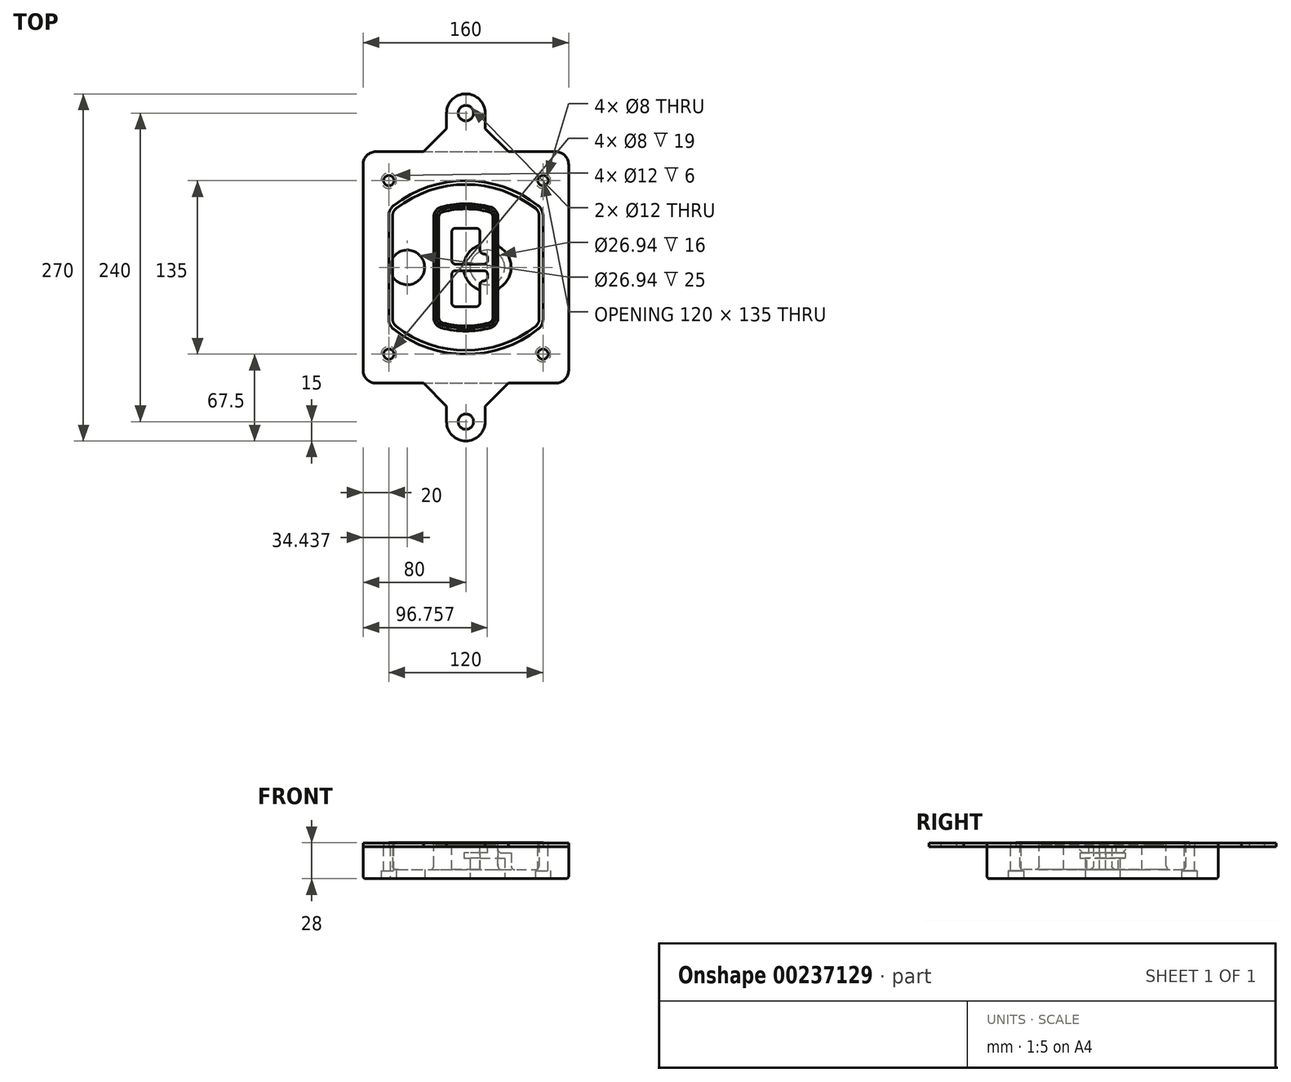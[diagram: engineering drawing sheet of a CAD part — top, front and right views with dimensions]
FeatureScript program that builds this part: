
annotation { "Feature Type Name" : "Feature", "Feature Type Description" : "" }
export const myFeature = defineFeature(function(context is Context, id is Id, definition is map)
    precondition{}
    {
        {
            var Q0;
            Q0=qCreatedBy(makeId("Top.planeOp"),FACE);
            var sketch = newSketch(context, id + "F0", { "sketchPlane" : qUnion([Q0])});
            skPoint(sketch, "E0.rect.middle", {"position": v(0, 0) * mm});
            skLineSegment(sketch, "E1.bottom", {"start": v(-70, -90) * mm, "end": v(70, -90) * mm});
            skLineSegment(sketch, "E1.top", {"start": v(-70, 90) * mm, "end": v(70, 90) * mm});
            skLineSegment(sketch, "E1.left", {"start": v(-80, -80) * mm, "end": v(-80, 80) * mm});
            skLineSegment(sketch, "E1.right", {"start": v(80, -80) * mm, "end": v(80, 80) * mm});
            skLineSegment(sketch, "E2", {"start": v(-80, 90) * mm, "end": v(80, -90) * mm, "construction": true});
            skLineSegment(sketch, "E3", {"start": v(80, 90) * mm, "end": v(-80, -90) * mm, "construction": true});
            skCircle(sketch, "E4", {"center": v(-60, 67.5) * mm, "radius": 4 * mm});
            skCircle(sketch, "E5", {"center": v(60, 67.5) * mm, "radius": 4 * mm});
            skCircle(sketch, "E6", {"center": v(60, -67.5) * mm, "radius": 4 * mm});
            skCircle(sketch, "E7", {"center": v(-60, -67.5) * mm, "radius": 4 * mm});
            skLineSegment(sketch, "E8", {"start": v(-60, 67.5) * mm, "end": v(60, 67.5) * mm, "construction": true});
            skLineSegment(sketch, "E9", {"start": v(60, 67.5) * mm, "end": v(60, -67.5) * mm, "construction": true});
            skLineSegment(sketch, "E10", {"start": v(60, -67.5) * mm, "end": v(-60, -67.5) * mm, "construction": true});
            skLineSegment(sketch, "E11", {"start": v(-60, -67.5) * mm, "end": v(-60, 67.5) * mm, "construction": true});
            skLineSegment(sketch, "E12", {"start": v(-60, 40.3) * mm, "end": v(-60, -40.3) * mm});
            skLineSegment(sketch, "E13", {"start": v(60, 40.3) * mm, "end": v(60, -40.3) * mm});
            skArc(sketch, "E14", {"start": v(56.15, 48.18) * mm, "mid": v(0, 67.5) * mm, "end": v(-56.15, 48.18) * mm});
            skArc(sketch, "E15", {"start": v(-56.15, -48.18) * mm, "mid": v(0, -67.5) * mm, "end": v(56.15, -48.18) * mm});
            skLineSegment(sketch, "E16", {"start": v(-60, 0) * mm, "end": v(60, 0) * mm, "construction": true});
            skPoint(sketch, "E17.visualSharp", {"position": v(-60, -45) * mm});
            skArc(sketch, "E17.filletArc", {"start": v(-60, -40.3) * mm, "mid": v(-58.99, -44.68) * mm, "end": v(-56.15, -48.18) * mm});
            skPoint(sketch, "E18.visualSharp", {"position": v(-60, 45) * mm});
            skArc(sketch, "E18.filletArc", {"start": v(-56.15, 48.18) * mm, "mid": v(-58.99, 44.68) * mm, "end": v(-60, 40.3) * mm});
            skPoint(sketch, "E19.visualSharp", {"position": v(60, 45) * mm});
            skArc(sketch, "E19.filletArc", {"start": v(60, 40.3) * mm, "mid": v(58.99, 44.68) * mm, "end": v(56.15, 48.18) * mm});
            skPoint(sketch, "E20.visualSharp", {"position": v(60, -45) * mm});
            skArc(sketch, "E20.filletArc", {"start": v(56.15, -48.18) * mm, "mid": v(58.99, -44.68) * mm, "end": v(60, -40.3) * mm});
            skPoint(sketch, "E21.visualSharp", {"position": v(-80, 90) * mm});
            skArc(sketch, "E21.filletArc", {"start": v(-70, 90) * mm, "mid": v(-77.07, 87.07) * mm, "end": v(-80, 80) * mm});
            skPoint(sketch, "E22.visualSharp", {"position": v(80, 90) * mm});
            skArc(sketch, "E22.filletArc", {"start": v(80, 80) * mm, "mid": v(77.07, 87.07) * mm, "end": v(70, 90) * mm});
            skPoint(sketch, "E23.visualSharp", {"position": v(80, -90) * mm});
            skArc(sketch, "E23.filletArc", {"start": v(70, -90) * mm, "mid": v(77.07, -87.07) * mm, "end": v(80, -80) * mm});
            skPoint(sketch, "E24.visualSharp", {"position": v(-80, -90) * mm});
            skArc(sketch, "E24.filletArc", {"start": v(-80, -80) * mm, "mid": v(-77.07, -87.07) * mm, "end": v(-70, -90) * mm});
            skArc(sketch, "E25.0", {"start": v(57, 40.3) * mm, "mid": v(56.3, 43.36) * mm, "end": v(54.3, 45.81) * mm});
            skLineSegment(sketch, "E25.1", {"start": v(57, 40.3) * mm, "end": v(57, -40.3) * mm});
            skArc(sketch, "E25.2", {"start": v(54.3, -45.81) * mm, "mid": v(56.3, -43.36) * mm, "end": v(57, -40.3) * mm});
            skArc(sketch, "E25.3", {"start": v(-54.3, -45.81) * mm, "mid": v(0, -64.5) * mm, "end": v(54.3, -45.81) * mm});
            skArc(sketch, "E25.4", {"start": v(-57, -40.3) * mm, "mid": v(-56.3, -43.36) * mm, "end": v(-54.3, -45.81) * mm});
            skArc(sketch, "E25.5", {"start": v(54.3, 45.81) * mm, "mid": v(0, 64.5) * mm, "end": v(-54.3, 45.81) * mm});
            skLineSegment(sketch, "E25.6", {"start": v(-57, 40.3) * mm, "end": v(-57, -40.3) * mm});
            skArc(sketch, "E25.7", {"start": v(-54.3, 45.81) * mm, "mid": v(-56.3, 43.36) * mm, "end": v(-57, 40.3) * mm});
            skArc(sketch, "E26.0", {"start": v(-58.62, 51.33) * mm, "mid": v(-62.58, 46.43) * mm, "end": v(-64, 40.3) * mm});
            skArc(sketch, "E26.1", {"start": v(58.62, 51.33) * mm, "mid": v(0, 71.5) * mm, "end": v(-58.62, 51.33) * mm});
            skArc(sketch, "E26.2", {"start": v(64, 40.3) * mm, "mid": v(62.58, 46.43) * mm, "end": v(58.62, 51.33) * mm});
            skLineSegment(sketch, "E26.3", {"start": v(64, 40.3) * mm, "end": v(64, -40.3) * mm});
            skArc(sketch, "E26.4", {"start": v(58.62, -51.33) * mm, "mid": v(62.58, -46.43) * mm, "end": v(64, -40.3) * mm});
            skLineSegment(sketch, "E26.5", {"start": v(-64, 40.3) * mm, "end": v(-64, -40.3) * mm});
            skArc(sketch, "E26.6", {"start": v(-58.62, -51.33) * mm, "mid": v(0, -71.5) * mm, "end": v(58.62, -51.33) * mm});
            skArc(sketch, "E26.7", {"start": v(-64, -40.3) * mm, "mid": v(-62.58, -46.43) * mm, "end": v(-58.62, -51.33) * mm});
            skSolve(sketch);
        }
        {
            var Q0;
            Q0=makeQuery(id+"F0.imprint","IMPRINT",FACE,{"disambiguationData":[TD([[makeQuery(id+"F0.imprint","IMPRINT",EDGE,{"derivedFrom":sQuery(id+"F0.wireOp",EDGE,"E1.bottom")}),1.0]])]});
            var Q1;
            Q1=makeQuery(id+"F0.imprint","IMPRINT",FACE,{"disambiguationData":[TD([[makeQuery(id+"F0.imprint","IMPRINT",EDGE,{"derivedFrom":sQuery(id+"F0.wireOp",EDGE,"E12")}),1.0]])]});
            var Q2;
            Q2=makeQuery(id+"F0.imprint","IMPRINT",FACE,{"disambiguationData":[TD([[makeQuery(id+"F0.imprint","IMPRINT",EDGE,{"derivedFrom":sQuery(id+"F0.wireOp",EDGE,"E25.0")}),1.0]])]});
            var Q3;
            Q3=makeQuery(id+"F0.imprint","IMPRINT",FACE,{"disambiguationData":[TD([[makeQuery(id+"F0.imprint","IMPRINT",EDGE,{"derivedFrom":sQuery(id+"F0.wireOp",EDGE,"E12")}),-1.0]])]});
            extrude(context, id + "F1", {"entities" : qUnion([Q0, Q1, Q2, Q3]), "oppositeDirection" : true, "depth" : 25 * mm});
        }
        {
            var Q0;
            Q0=makeQuery(id+"F0.imprint","IMPRINT",FACE,{"disambiguationData":[TD([[makeQuery(id+"F0.imprint","IMPRINT",EDGE,{"derivedFrom":sQuery(id+"F0.wireOp",EDGE,"E12")}),1.0]])]});
            extrude(context, id + "F2", {"entities" : qUnion([Q0]), "operationType" : NewBodyOperationType.ADD, "depth" : 3 * mm});
        }
        {
            var Q0;
            Q0=makeQuery(id+"F0.imprint","IMPRINT",FACE,{"disambiguationData":[TD([[makeQuery(id+"F0.imprint","IMPRINT",EDGE,{"derivedFrom":sQuery(id+"F0.wireOp",EDGE,"E25.0")}),1.0]])]});
            extrude(context, id + "F3", {"entities" : qUnion([Q0]), "operationType" : NewBodyOperationType.REMOVE, "oppositeDirection" : true, "depth" : 18 * mm});
        }
        {
            var Q0;
            Q0=makeQuery(id+"F2.opExtrude","CAP_FACE",FACE,{"disambiguationData":[OSD([sQuery(id+"F0.wireOp",EDGE,"E12"),sQuery(id+"F0.wireOp",EDGE,"E13"),sQuery(id+"F0.wireOp",EDGE,"E14"),sQuery(id+"F0.wireOp",EDGE,"E15"),sQuery(id+"F0.wireOp",EDGE,"E17.filletArc"),sQuery(id+"F0.wireOp",EDGE,"E18.filletArc"),sQuery(id+"F0.wireOp",EDGE,"E19.filletArc"),sQuery(id+"F0.wireOp",EDGE,"E20.filletArc"),sQuery(id+"F0.wireOp",EDGE,"E25.0"),sQuery(id+"F0.wireOp",EDGE,"E25.1"),sQuery(id+"F0.wireOp",EDGE,"E25.2"),sQuery(id+"F0.wireOp",EDGE,"E25.3"),sQuery(id+"F0.wireOp",EDGE,"E25.4"),sQuery(id+"F0.wireOp",EDGE,"E25.5"),sQuery(id+"F0.wireOp",EDGE,"E25.6"),sQuery(id+"F0.wireOp",EDGE,"E25.7")])],"isStart":false});
            var sketch = newSketch(context, id + "F4", { "sketchPlane" : qUnion([Q0])});
            skArc(sketch, "E27.0", {"start": v(-19.08, -46.97) * mm, "mid": v(0, -49.5) * mm, "end": v(19.08, -46.97) * mm});
            skArc(sketch, "E28.0", {"start": v(19.08, 46.97) * mm, "mid": v(0, 49.5) * mm, "end": v(-19.08, 46.97) * mm});
            skLineSegment(sketch, "E29", {"start": v(-25, 39.25) * mm, "end": v(-25, -39.25) * mm});
            skLineSegment(sketch, "E30", {"start": v(25, 39.25) * mm, "end": v(25, -39.25) * mm});
            skLineSegment(sketch, "E31", {"start": v(-25, 45.1) * mm, "end": v(25, 45.1) * mm, "construction": true});
            skLineSegment(sketch, "E32", {"start": v(-25, -45.1) * mm, "end": v(25, -45.1) * mm, "construction": true});
            skPoint(sketch, "E33.visualSharp", {"position": v(-25, 45.1) * mm});
            skArc(sketch, "E33.filletArc", {"start": v(-19.08, 46.97) * mm, "mid": v(-23.35, 44.11) * mm, "end": v(-25, 39.25) * mm});
            skPoint(sketch, "E34.visualSharp", {"position": v(25, 45.1) * mm});
            skArc(sketch, "E34.filletArc", {"start": v(25, 39.25) * mm, "mid": v(23.35, 44.11) * mm, "end": v(19.08, 46.97) * mm});
            skPoint(sketch, "E35.visualSharp", {"position": v(25, -45.1) * mm});
            skArc(sketch, "E35.filletArc", {"start": v(19.08, -46.97) * mm, "mid": v(23.35, -44.11) * mm, "end": v(25, -39.25) * mm});
            skPoint(sketch, "E36.visualSharp", {"position": v(-25, -45.1) * mm});
            skArc(sketch, "E36.filletArc", {"start": v(-25, -39.25) * mm, "mid": v(-23.35, -44.11) * mm, "end": v(-19.08, -46.97) * mm});
            skArc(sketch, "E37.0", {"start": v(54.3, 45.81) * mm, "mid": v(0, 64.5) * mm, "end": v(-54.3, 45.81) * mm});
            skArc(sketch, "E37.1", {"start": v(-54.3, 45.81) * mm, "mid": v(-56.3, 43.36) * mm, "end": v(-57, 40.3) * mm});
            skLineSegment(sketch, "E37.2", {"start": v(-57, 40.3) * mm, "end": v(-57, -40.3) * mm});
            skArc(sketch, "E37.3", {"start": v(-57, -40.3) * mm, "mid": v(-56.3, -43.36) * mm, "end": v(-54.3, -45.81) * mm});
            skArc(sketch, "E37.4", {"start": v(-54.3, -45.81) * mm, "mid": v(0, -64.5) * mm, "end": v(54.3, -45.81) * mm});
            skArc(sketch, "E37.5", {"start": v(54.3, -45.81) * mm, "mid": v(56.3, -43.36) * mm, "end": v(57, -40.3) * mm});
            skLineSegment(sketch, "E37.6", {"start": v(57, 40.3) * mm, "end": v(57, -40.3) * mm});
            skArc(sketch, "E37.7", {"start": v(57, 40.3) * mm, "mid": v(56.3, 43.36) * mm, "end": v(54.3, 45.81) * mm});
            skLineSegment(sketch, "E38.0", {"start": v(23, 39.25) * mm, "end": v(23, -39.25) * mm});
            skArc(sketch, "E38.1", {"start": v(18.56, -45.04) * mm, "mid": v(21.76, -42.9) * mm, "end": v(23, -39.25) * mm});
            skArc(sketch, "E38.2", {"start": v(-18.56, -45.04) * mm, "mid": v(0, -47.5) * mm, "end": v(18.56, -45.04) * mm});
            skArc(sketch, "E38.3", {"start": v(-23, -39.25) * mm, "mid": v(-21.76, -42.9) * mm, "end": v(-18.56, -45.04) * mm});
            skLineSegment(sketch, "E38.4", {"start": v(-23, 39.25) * mm, "end": v(-23, -39.25) * mm});
            skArc(sketch, "E38.5", {"start": v(23, 39.25) * mm, "mid": v(21.76, 42.9) * mm, "end": v(18.56, 45.04) * mm});
            skArc(sketch, "E38.6", {"start": v(-18.56, 45.04) * mm, "mid": v(-21.76, 42.9) * mm, "end": v(-23, 39.25) * mm});
            skArc(sketch, "E38.7", {"start": v(18.56, 45.04) * mm, "mid": v(0, 47.5) * mm, "end": v(-18.56, 45.04) * mm});
            skArc(sketch, "E39.0", {"start": v(21, 39.25) * mm, "mid": v(20.18, 41.68) * mm, "end": v(18.04, 43.1) * mm});
            skLineSegment(sketch, "E39.1", {"start": v(21, 39.25) * mm, "end": v(21, -39.25) * mm});
            skArc(sketch, "E39.2", {"start": v(18.04, -43.1) * mm, "mid": v(20.18, -41.68) * mm, "end": v(21, -39.25) * mm});
            skArc(sketch, "E39.3", {"start": v(-18.04, -43.1) * mm, "mid": v(0, -45.5) * mm, "end": v(18.04, -43.1) * mm});
            skArc(sketch, "E39.4", {"start": v(-21, -39.25) * mm, "mid": v(-20.18, -41.68) * mm, "end": v(-18.04, -43.1) * mm});
            skArc(sketch, "E39.5", {"start": v(18.04, 43.1) * mm, "mid": v(0, 45.5) * mm, "end": v(-18.04, 43.1) * mm});
            skLineSegment(sketch, "E39.6", {"start": v(-21, 39.25) * mm, "end": v(-21, -39.25) * mm});
            skArc(sketch, "E39.7", {"start": v(-18.04, 43.1) * mm, "mid": v(-20.18, 41.68) * mm, "end": v(-21, 39.25) * mm});
            skLineSegment(sketch, "E40", {"start": v(-25, 0) * mm, "end": v(25, 0) * mm, "construction": true});
            skLineSegment(sketch, "E41", {"start": v(-11, 5.5) * mm, "end": v(-11, 27.5) * mm});
            skLineSegment(sketch, "E42", {"start": v(-8, 30.5) * mm, "end": v(8, 30.5) * mm});
            skLineSegment(sketch, "E43", {"start": v(11, 27.5) * mm, "end": v(11, 13.5) * mm});
            skLineSegment(sketch, "E44", {"start": v(14, 10.5) * mm, "end": v(14, 10.5) * mm});
            skLineSegment(sketch, "E45", {"start": v(17, 7.5) * mm, "end": v(17, 5.5) * mm});
            skLineSegment(sketch, "E46", {"start": v(14, 2.5) * mm, "end": v(-8, 2.5) * mm});
            skPoint(sketch, "E47.visualSharp", {"position": v(-11, 30.5) * mm});
            skArc(sketch, "E47.filletArc", {"start": v(-8, 30.5) * mm, "mid": v(-10.12, 29.62) * mm, "end": v(-11, 27.5) * mm});
            skPoint(sketch, "E48.visualSharp", {"position": v(11, 30.5) * mm});
            skArc(sketch, "E48.filletArc", {"start": v(11, 27.5) * mm, "mid": v(10.12, 29.62) * mm, "end": v(8, 30.5) * mm});
            skPoint(sketch, "E49.visualSharp", {"position": v(11, 10.5) * mm});
            skArc(sketch, "E49.filletArc", {"start": v(11, 13.5) * mm, "mid": v(11.88, 11.38) * mm, "end": v(14, 10.5) * mm});
            skPoint(sketch, "E50.visualSharp", {"position": v(17, 10.5) * mm});
            skArc(sketch, "E50.filletArc", {"start": v(17, 7.5) * mm, "mid": v(16.12, 9.62) * mm, "end": v(14, 10.5) * mm});
            skPoint(sketch, "E51.visualSharp", {"position": v(17, 2.5) * mm});
            skArc(sketch, "E51.filletArc", {"start": v(14, 2.5) * mm, "mid": v(16.12, 3.38) * mm, "end": v(17, 5.5) * mm});
            skPoint(sketch, "E52.visualSharp", {"position": v(-11, 2.5) * mm});
            skArc(sketch, "E52.filletArc", {"start": v(-11, 5.5) * mm, "mid": v(-10.12, 3.38) * mm, "end": v(-8, 2.5) * mm});
            skLineSegment(sketch, "E53.0.MirrorCS", {"start": v(14, -2.5) * mm, "end": v(-8, -2.5) * mm});
            skArc(sketch, "E54.0.MirrorCS", {"start": v(-11, -5.5) * mm, "mid": v(-10.12, -3.38) * mm, "end": v(-8, -2.5) * mm});
            skLineSegment(sketch, "E55.0.MirrorCS", {"start": v(-11, -5.5) * mm, "end": v(-11, -27.5) * mm});
            skArc(sketch, "E56.0.MirrorCS", {"start": v(-8, -30.5) * mm, "mid": v(-10.12, -29.62) * mm, "end": v(-11, -27.5) * mm});
            skLineSegment(sketch, "E57.0.MirrorCS", {"start": v(-8, -30.5) * mm, "end": v(8, -30.5) * mm});
            skArc(sketch, "E58.0.MirrorCS", {"start": v(11, -27.5) * mm, "mid": v(10.12, -29.62) * mm, "end": v(8, -30.5) * mm});
            skLineSegment(sketch, "E59.0.MirrorCS", {"start": v(11, -27.5) * mm, "end": v(11, -13.5) * mm});
            skArc(sketch, "E60.0.MirrorCS", {"start": v(11, -13.5) * mm, "mid": v(11.88, -11.38) * mm, "end": v(14, -10.5) * mm});
            skArc(sketch, "E61.0.MirrorCS", {"start": v(17, -7.5) * mm, "mid": v(16.12, -9.62) * mm, "end": v(14, -10.5) * mm});
            skLineSegment(sketch, "E62.0.MirrorCS", {"start": v(17, -7.5) * mm, "end": v(17, -5.5) * mm});
            skArc(sketch, "E63.0.MirrorCS", {"start": v(14, -2.5) * mm, "mid": v(16.12, -3.38) * mm, "end": v(17, -5.5) * mm});
            skSolve(sketch);
        }
        {
            var Q0;
            Q0=makeQuery(id+"F4.imprint","IMPRINT",FACE,{"disambiguationData":[TD([[makeQuery(id+"F4.imprint","IMPRINT",EDGE,{"derivedFrom":sQuery(id+"F4.wireOp",EDGE,"E27.0")}),1.0]])]});
            var Q1;
            Q1=makeQuery(id+"F4.imprint","IMPRINT",FACE,{"disambiguationData":[TD([[makeQuery(id+"F4.imprint","IMPRINT",EDGE,{"derivedFrom":sQuery(id+"F4.wireOp",EDGE,"E38.0")}),-1.0]])]});
            var Q2;
            Q2=makeQuery(id+"F4.imprint","IMPRINT",FACE,{"disambiguationData":[TD([[makeQuery(id+"F4.imprint","IMPRINT",EDGE,{"derivedFrom":sQuery(id+"F4.wireOp",EDGE,"E39.0")}),1.0]])]});
            extrude(context, id + "F5", {"entities" : qUnion([Q0, Q1, Q2]), "operationType" : NewBodyOperationType.ADD, "endBound" : BoundingType.UP_TO_NEXT, "oppositeDirection" : true, "depth" : 25 * mm});
        }
        {
            var Q0;
            Q0=makeQuery(id+"F4.imprint","IMPRINT",FACE,{"disambiguationData":[TD([[makeQuery(id+"F4.imprint","IMPRINT",EDGE,{"derivedFrom":sQuery(id+"F4.wireOp",EDGE,"E38.0")}),-1.0]])]});
            extrude(context, id + "F6", {"entities" : qUnion([Q0]), "operationType" : NewBodyOperationType.REMOVE, "oppositeDirection" : true, "depth" : 2 * mm});
        }
        {
            var Q0;
            Q0=makeQuery(id+"F1.opExtrude","CAP_FACE",FACE,{"disambiguationData":[OSD([sQuery(id+"F0.wireOp",EDGE,"E1.bottom"),sQuery(id+"F0.wireOp",EDGE,"E1.top"),sQuery(id+"F0.wireOp",EDGE,"E1.left"),sQuery(id+"F0.wireOp",EDGE,"E1.right"),sQuery(id+"F0.wireOp",EDGE,"E4"),sQuery(id+"F0.wireOp",EDGE,"E5"),sQuery(id+"F0.wireOp",EDGE,"E6"),sQuery(id+"F0.wireOp",EDGE,"E7"),sQuery(id+"F0.wireOp",EDGE,"E21.filletArc"),sQuery(id+"F0.wireOp",EDGE,"E22.filletArc"),sQuery(id+"F0.wireOp",EDGE,"E23.filletArc"),sQuery(id+"F0.wireOp",EDGE,"E24.filletArc")])],"isStart":false});
            var sketch = newSketch(context, id + "F7", { "sketchPlane" : qUnion([Q0])});
            skCircle(sketch, "E64", {"center": v(16.76, 0) * mm, "radius": 13.47 * mm});
            skCircle(sketch, "E65", {"center": v(-45.56, 0) * mm, "radius": 13.47 * mm});
            skLineSegment(sketch, "E66", {"start": v(80, 0) * mm, "end": v(-80, 0) * mm});
            skCircle(sketch, "E67", {"center": v(16.76, 0) * mm, "radius": 18.47 * mm});
            skCircle(sketch, "E68", {"center": v(60, -67.5) * mm, "radius": 6 * mm});
            skCircle(sketch, "E69", {"center": v(-60, -67.5) * mm, "radius": 6 * mm});
            skCircle(sketch, "E70", {"center": v(-60, 67.5) * mm, "radius": 6 * mm});
            skCircle(sketch, "E71", {"center": v(60, 67.5) * mm, "radius": 6 * mm});
            skSolve(sketch);
        }
        {
            var Q0;
            {var subQ1=sQuery(id+"F7.wireOp",EDGE,"E66");var subQ4=sQuery(id+"F7.wireOp",EDGE,"E64");var subQ6=makeQuery(id+"F7.imprint","INTERSECT",VERTEX,{"disambiguationData":[OD(0.0)],"derivedFrom":[subQ4,subQ1]});Q0=makeQuery(id+"F7.imprint","IMPRINT",FACE,{"disambiguationData":[TD([[makeQuery(id+"F7.imprint","IMPRINT",EDGE,{"disambiguationData":[TD([[subQ6,-1.0]])],"derivedFrom":subQ4}),-1.0]])]});}
            var Q1;
            {var subQ0=sQuery(id+"F7.wireOp",EDGE,"E66");var subQ1=sQuery(id+"F7.wireOp",EDGE,"E64");var subQ3=makeQuery(id+"F7.imprint","INTERSECT",VERTEX,{"disambiguationData":[OD(0.0)],"derivedFrom":[subQ1,subQ0]});Q1=makeQuery(id+"F7.imprint","IMPRINT",FACE,{"disambiguationData":[TD([[makeQuery(id+"F7.imprint","IMPRINT",EDGE,{"disambiguationData":[TD([[subQ3,-1.0]])],"derivedFrom":subQ1}),1.0]])]});}
            var Q2;
            {var subQ0=sQuery(id+"F7.wireOp",EDGE,"E66");var subQ1=sQuery(id+"F7.wireOp",EDGE,"E64");var subQ3=makeQuery(id+"F7.imprint","INTERSECT",VERTEX,{"disambiguationData":[OD(0.0)],"derivedFrom":[subQ1,subQ0]});Q2=makeQuery(id+"F7.imprint","IMPRINT",FACE,{"disambiguationData":[TD([[makeQuery(id+"F7.imprint","IMPRINT",EDGE,{"disambiguationData":[TD([[subQ3,1.0]])],"derivedFrom":subQ1}),1.0]])]});}
            var Q3;
            {var subQ1=sQuery(id+"F7.wireOp",EDGE,"E66");var subQ4=sQuery(id+"F7.wireOp",EDGE,"E64");var subQ6=makeQuery(id+"F7.imprint","INTERSECT",VERTEX,{"disambiguationData":[OD(0.0)],"derivedFrom":[subQ4,subQ1]});Q3=makeQuery(id+"F7.imprint","IMPRINT",FACE,{"disambiguationData":[TD([[makeQuery(id+"F7.imprint","IMPRINT",EDGE,{"disambiguationData":[TD([[subQ6,1.0]])],"derivedFrom":subQ4}),-1.0]])]});}
            extrude(context, id + "F8", {"entities" : qUnion([Q0, Q1, Q2, Q3]), "operationType" : NewBodyOperationType.ADD, "oppositeDirection" : true, "depth" : 20 * mm});
        }
        {
            var Q0;
            {var subQ0=sQuery(id+"F7.wireOp",EDGE,"E66");var subQ1=sQuery(id+"F7.wireOp",EDGE,"E64");var subQ3=makeQuery(id+"F7.imprint","INTERSECT",VERTEX,{"disambiguationData":[OD(0.0)],"derivedFrom":[subQ1,subQ0]});Q0=makeQuery(id+"F7.imprint","IMPRINT",FACE,{"disambiguationData":[TD([[makeQuery(id+"F7.imprint","IMPRINT",EDGE,{"disambiguationData":[TD([[subQ3,-1.0]])],"derivedFrom":subQ1}),1.0]])]});}
            var Q1;
            {var subQ0=sQuery(id+"F7.wireOp",EDGE,"E66");var subQ1=sQuery(id+"F7.wireOp",EDGE,"E64");var subQ3=makeQuery(id+"F7.imprint","INTERSECT",VERTEX,{"disambiguationData":[OD(0.0)],"derivedFrom":[subQ1,subQ0]});Q1=makeQuery(id+"F7.imprint","IMPRINT",FACE,{"disambiguationData":[TD([[makeQuery(id+"F7.imprint","IMPRINT",EDGE,{"disambiguationData":[TD([[subQ3,1.0]])],"derivedFrom":subQ1}),1.0]])]});}
            extrude(context, id + "F9", {"entities" : qUnion([Q0, Q1]), "operationType" : NewBodyOperationType.REMOVE, "oppositeDirection" : true, "depth" : 16 * mm});
        }
        {
            var Q0;
            {var subQ0=sQuery(id+"F7.wireOp",EDGE,"E66");var subQ1=sQuery(id+"F7.wireOp",EDGE,"E65");var subQ3=makeQuery(id+"F7.imprint","INTERSECT",VERTEX,{"disambiguationData":[OD(0.0)],"derivedFrom":[subQ1,subQ0]});Q0=makeQuery(id+"F7.imprint","IMPRINT",FACE,{"disambiguationData":[TD([[makeQuery(id+"F7.imprint","IMPRINT",EDGE,{"disambiguationData":[TD([[subQ3,-1.0]])],"derivedFrom":subQ1}),1.0]])]});}
            var Q1;
            {var subQ0=sQuery(id+"F7.wireOp",EDGE,"E66");var subQ1=sQuery(id+"F7.wireOp",EDGE,"E65");var subQ3=makeQuery(id+"F7.imprint","INTERSECT",VERTEX,{"disambiguationData":[OD(0.0)],"derivedFrom":[subQ1,subQ0]});Q1=makeQuery(id+"F7.imprint","IMPRINT",FACE,{"disambiguationData":[TD([[makeQuery(id+"F7.imprint","IMPRINT",EDGE,{"disambiguationData":[TD([[subQ3,1.0]])],"derivedFrom":subQ1}),1.0]])]});}
            extrude(context, id + "F10", {"entities" : qUnion([Q0, Q1]), "operationType" : NewBodyOperationType.REMOVE, "oppositeDirection" : true, "depth" : 25 * mm});
        }
        {
            var Q0;
            Q0=makeQuery(id+"F7.imprint","IMPRINT",FACE,{"disambiguationData":[TD([[makeQuery(id+"F7.imprint","IMPRINT",EDGE,{"derivedFrom":sQuery(id+"F7.wireOp",EDGE,"E68")}),1.0]])]});
            var Q1;
            Q1=makeQuery(id+"F7.imprint","IMPRINT",FACE,{"disambiguationData":[TD([[makeQuery(id+"F7.imprint","IMPRINT",EDGE,{"derivedFrom":makeQuery(id+"F1.opExtrude","CAP_EDGE",EDGE,{"disambiguationData":[OSD([sQuery(id+"F0.wireOp",EDGE,"E5")])],"isStart":false})}),-1.0]])]});
            var Q2;
            Q2=makeQuery(id+"F7.imprint","IMPRINT",FACE,{"disambiguationData":[TD([[makeQuery(id+"F7.imprint","IMPRINT",EDGE,{"derivedFrom":sQuery(id+"F7.wireOp",EDGE,"E69")}),1.0]])]});
            var Q3;
            Q3=makeQuery(id+"F7.imprint","IMPRINT",FACE,{"disambiguationData":[TD([[makeQuery(id+"F7.imprint","IMPRINT",EDGE,{"derivedFrom":makeQuery(id+"F1.opExtrude","CAP_EDGE",EDGE,{"disambiguationData":[OSD([sQuery(id+"F0.wireOp",EDGE,"E4")])],"isStart":false})}),-1.0]])]});
            var Q4;
            Q4=makeQuery(id+"F7.imprint","IMPRINT",FACE,{"disambiguationData":[TD([[makeQuery(id+"F7.imprint","IMPRINT",EDGE,{"derivedFrom":sQuery(id+"F7.wireOp",EDGE,"E70")}),1.0]])]});
            var Q5;
            Q5=makeQuery(id+"F7.imprint","IMPRINT",FACE,{"disambiguationData":[TD([[makeQuery(id+"F7.imprint","IMPRINT",EDGE,{"derivedFrom":makeQuery(id+"F1.opExtrude","CAP_EDGE",EDGE,{"disambiguationData":[OSD([sQuery(id+"F0.wireOp",EDGE,"E7")])],"isStart":false})}),-1.0]])]});
            var Q6;
            Q6=makeQuery(id+"F7.imprint","IMPRINT",FACE,{"disambiguationData":[TD([[makeQuery(id+"F7.imprint","IMPRINT",EDGE,{"derivedFrom":sQuery(id+"F7.wireOp",EDGE,"E71")}),1.0]])]});
            var Q7;
            Q7=makeQuery(id+"F7.imprint","IMPRINT",FACE,{"disambiguationData":[TD([[makeQuery(id+"F7.imprint","IMPRINT",EDGE,{"derivedFrom":makeQuery(id+"F1.opExtrude","CAP_EDGE",EDGE,{"disambiguationData":[OSD([sQuery(id+"F0.wireOp",EDGE,"E6")])],"isStart":false})}),-1.0]])]});
            extrude(context, id + "F11", {"entities" : qUnion([Q0, Q1, Q2, Q3, Q4, Q5, Q6, Q7]), "operationType" : NewBodyOperationType.REMOVE, "oppositeDirection" : true, "depth" : 6 * mm});
        }
        {
            var Q0;
            Q0=makeQuery(id+"F9.boolean.opBoolean","COPY",FACE,{"derivedFrom":makeQuery(id+"F9.opExtrude","CAP_FACE",FACE,{"disambiguationData":[OSD([sQuery(id+"F7.wireOp",EDGE,"E64")])],"isStart":false})});
            var sketch = newSketch(context, id + "F12", { "sketchPlane" : qUnion([Q0])});
            skArc(sketch, "E72.0", {"start": v(11, 17.55) * mm, "mid": v(2.57, 11.82) * mm, "end": v(-1.54, 2.5) * mm});
            skArc(sketch, "E72.1", {"start": v(-1.54, -2.5) * mm, "mid": v(2.57, -11.82) * mm, "end": v(11, -17.55) * mm});
            skLineSegment(sketch, "E73", {"start": v(-1.54, -2.5) * mm, "end": v(14, -2.5) * mm});
            skLineSegment(sketch, "E74.0", {"start": v(14, 2.5) * mm, "end": v(-1.54, 2.5) * mm});
            skArc(sketch, "E74.1", {"start": v(14, 2.5) * mm, "mid": v(16.12, 3.38) * mm, "end": v(17, 5.5) * mm});
            skLineSegment(sketch, "E74.2", {"start": v(17, 7.5) * mm, "end": v(17, 5.5) * mm});
            skArc(sketch, "E74.3", {"start": v(17, 7.5) * mm, "mid": v(16.12, 9.62) * mm, "end": v(14, 10.5) * mm});
            skArc(sketch, "E74.4", {"start": v(11, 13.5) * mm, "mid": v(11.88, 11.38) * mm, "end": v(14, 10.5) * mm});
            skLineSegment(sketch, "E74.5", {"start": v(11, 17.55) * mm, "end": v(11, 13.5) * mm});
            skLineSegment(sketch, "E74.7", {"start": v(14, -2.5) * mm, "end": v(-1.54, -2.5) * mm});
            skArc(sketch, "E74.8", {"start": v(14, -2.5) * mm, "mid": v(16.12, -3.38) * mm, "end": v(17, -5.5) * mm});
            skLineSegment(sketch, "E74.9", {"start": v(17, -7.5) * mm, "end": v(17, -5.5) * mm});
            skArc(sketch, "E74.10", {"start": v(17, -7.5) * mm, "mid": v(16.12, -9.62) * mm, "end": v(14, -10.5) * mm});
            skArc(sketch, "E74.11", {"start": v(11, -13.5) * mm, "mid": v(11.88, -11.38) * mm, "end": v(14, -10.5) * mm});
            skLineSegment(sketch, "E74.12", {"start": v(11, -17.55) * mm, "end": v(11, -13.5) * mm});
            skPoint(sketch, "E75.orphan", {"position": v(11, -27.5) * mm});
            skPoint(sketch, "E76.orphan", {"position": v(-8, -2.5) * mm});
            skPoint(sketch, "E77.orphan", {"position": v(-8, 2.5) * mm});
            skPoint(sketch, "E78.orphan", {"position": v(11, 27.5) * mm});
            skSolve(sketch);
        }
        {
            var Q0;
            {var subQ7=sQuery(id+"F12.wireOp",EDGE,"E72.0");var subQ14=sQuery(id+"F12.wireOp",EDGE,"E72.1");var subQ16=sQuery(id+"F12.wireOp",EDGE,"E74.1");var subQ18=sQuery(id+"F12.wireOp",EDGE,"E74.8");Q0=qUnion([makeQuery(id+"F12.imprint","IMPRINT",FACE,{"disambiguationData":[TD([[makeQuery(id+"F12.imprint","IMPRINT",EDGE,{"derivedFrom":subQ7}),1.0]])]}),makeQuery(id+"F12.imprint","IMPRINT",FACE,{"disambiguationData":[TD([[makeQuery(id+"F12.imprint","IMPRINT",EDGE,{"derivedFrom":subQ14}),1.0]])]}),makeQuery(id+"F12.imprint","IMPRINT",FACE,{"disambiguationData":[TD([[makeQuery(id+"F12.imprint","IMPRINT",EDGE,{"derivedFrom":subQ16}),1.0]])]}),makeQuery(id+"F12.imprint","IMPRINT",FACE,{"disambiguationData":[TD([[makeQuery(id+"F12.imprint","IMPRINT",EDGE,{"derivedFrom":subQ18}),-1.0]])]})]);}
            var Q1;
            Q1=makeQuery(id+"F5.boolean.opBoolean","SPLIT",FACE,{"disambiguationData":[TD([makeQuery(id+"F5.opExtrude","SWEPT_FACE",FACE,{"disambiguationData":[OSD([sQuery(id+"F4.wireOp",EDGE,"E41")])]})])],"derivedFrom":makeQuery(id+"F3.boolean.opBoolean","COPY",FACE,{"derivedFrom":makeQuery(id+"F3.opExtrude","CAP_FACE",FACE,{"disambiguationData":[OSD([sQuery(id+"F0.wireOp",EDGE,"E25.0"),sQuery(id+"F0.wireOp",EDGE,"E25.1"),sQuery(id+"F0.wireOp",EDGE,"E25.2"),sQuery(id+"F0.wireOp",EDGE,"E25.3"),sQuery(id+"F0.wireOp",EDGE,"E25.4"),sQuery(id+"F0.wireOp",EDGE,"E25.5"),sQuery(id+"F0.wireOp",EDGE,"E25.6"),sQuery(id+"F0.wireOp",EDGE,"E25.7")])],"isStart":false})})});
            extrude(context, id + "F13", {"entities" : qUnion([Q0]), "operationType" : NewBodyOperationType.REMOVE, "endBound" : BoundingType.UP_TO_SURFACE, "endBoundEntityFace" : qUnion([Q1]), "depth" : 25 * mm});
        }
        {
            var Q0;
            Q0=makeQuery(id+"F3.boolean.opBoolean","COPY",EDGE,{"derivedFrom":makeQuery(id+"F3.opExtrude","CAP_EDGE",EDGE,{"disambiguationData":[OSD([sQuery(id+"F0.wireOp",EDGE,"E25.6")])],"isStart":false})});
            var Q1;
            Q1=makeQuery(id+"F8.boolean.opBoolean","INTERSECT",EDGE,{"derivedFrom":[makeQuery(id+"F5.opExtrude","SWEPT_FACE",FACE,{"disambiguationData":[OSD([sQuery(id+"F4.wireOp",EDGE,"E30")])]}),makeQuery(id+"F8.opExtrude","CAP_FACE",FACE,{"disambiguationData":[OSD([sQuery(id+"F7.wireOp",EDGE,"E67")])],"isStart":false})]});
            var Q2;
            Q2=makeQuery(id+"F8.boolean.opBoolean","INTERSECT",EDGE,{"disambiguationData":[OD(1.0)],"derivedFrom":[makeQuery(id+"F5.opExtrude","SWEPT_FACE",FACE,{"disambiguationData":[OSD([sQuery(id+"F4.wireOp",EDGE,"E30")])]}),makeQuery(id+"F8.opExtrude","SWEPT_FACE",FACE,{"disambiguationData":[OSD([sQuery(id+"F7.wireOp",EDGE,"E67")])]})]});
            var Q3;
            {var subQ0=sQuery(id+"F4.wireOp",EDGE,"E30");Q3=makeQuery(id+"F8.boolean.opBoolean","SPLIT",EDGE,{"disambiguationData":[TD([makeQuery(id+"F5.opExtrude","SWEPT_FACE",FACE,{"disambiguationData":[OSD([sQuery(id+"F4.wireOp",EDGE,"E35.filletArc")])]})])],"derivedFrom":makeQuery(id+"F5.opExtrude","CAP_EDGE",EDGE,{"disambiguationData":[OSD([subQ0])],"isStart":false})});}
            var Q4;
            {var subQ0=sQuery(id+"F0.wireOp",EDGE,"E25.7");var subQ1=sQuery(id+"F0.wireOp",EDGE,"E25.1");var subQ2=sQuery(id+"F0.wireOp",EDGE,"E25.6");var subQ3=sQuery(id+"F0.wireOp",EDGE,"E25.5");var subQ4=sQuery(id+"F0.wireOp",EDGE,"E25.4");var subQ5=sQuery(id+"F0.wireOp",EDGE,"E25.0");var subQ6=sQuery(id+"F0.wireOp",EDGE,"E25.2");var subQ7=sQuery(id+"F0.wireOp",EDGE,"E25.3");Q4=makeQuery(id+"F8.boolean.opBoolean","INTERSECT",EDGE,{"derivedFrom":[makeQuery(id+"F5.boolean.opBoolean","SPLIT",FACE,{"disambiguationData":[TD([makeQuery(id+"F2.opExtrude","SWEPT_FACE",FACE,{"disambiguationData":[OSD([subQ5])]})])],"derivedFrom":makeQuery(id+"F3.boolean.opBoolean","COPY",FACE,{"derivedFrom":makeQuery(id+"F3.opExtrude","CAP_FACE",FACE,{"disambiguationData":[OSD([subQ5,subQ1,subQ6,subQ7,subQ4,subQ3,subQ2,subQ0])],"isStart":false})})}),makeQuery(id+"F8.opExtrude","SWEPT_FACE",FACE,{"disambiguationData":[OSD([sQuery(id+"F7.wireOp",EDGE,"E67")])]})]});}
            var Q5;
            Q5=makeQuery(id+"F8.boolean.opBoolean","INTERSECT",EDGE,{"disambiguationData":[OD(0.0)],"derivedFrom":[makeQuery(id+"F5.opExtrude","SWEPT_FACE",FACE,{"disambiguationData":[OSD([sQuery(id+"F4.wireOp",EDGE,"E30")])]}),makeQuery(id+"F8.opExtrude","SWEPT_FACE",FACE,{"disambiguationData":[OSD([sQuery(id+"F7.wireOp",EDGE,"E67")])]})]});
            fillet(context, id + "F14", {"entities" : qUnion([Q0, Q1, Q2, Q3, Q4, Q5]), "radius" : 3 * mm, "tangentPropagation" : true, "allowEdgeOverflow" : false});
        }
        {
            var Q0;
            Q0=makeQuery(id+"F1.opExtrude","CAP_EDGE",EDGE,{"disambiguationData":[OSD([sQuery(id+"F0.wireOp",EDGE,"E1.bottom")])],"isStart":false});
            fillet(context, id + "F15", {"entities" : qUnion([Q0]), "radius" : 2 * mm, "tangentPropagation" : true, "allowEdgeOverflow" : false});
        }
        {
            var Q0;
            {var subQ0=sQuery(id+"F0.wireOp",EDGE,"E22.filletArc");var subQ1=sQuery(id+"F0.wireOp",EDGE,"E7");var subQ2=sQuery(id+"F0.wireOp",EDGE,"E6");var subQ3=sQuery(id+"F0.wireOp",EDGE,"E5");var subQ4=sQuery(id+"F0.wireOp",EDGE,"E4");var subQ5=sQuery(id+"F0.wireOp",EDGE,"E1.bottom");var subQ6=sQuery(id+"F0.wireOp",EDGE,"E21.filletArc");var subQ7=sQuery(id+"F0.wireOp",EDGE,"E1.top");var subQ8=sQuery(id+"F0.wireOp",EDGE,"E1.left");var subQ9=sQuery(id+"F0.wireOp",EDGE,"E1.right");var subQ10=sQuery(id+"F0.wireOp",EDGE,"E23.filletArc");var subQ11=sQuery(id+"F0.wireOp",EDGE,"E24.filletArc");Q0=makeQuery(id+"F2.boolean.opBoolean","SPLIT",FACE,{"disambiguationData":[TD([makeQuery(id+"F1.opExtrude","SWEPT_FACE",FACE,{"disambiguationData":[OSD([subQ5])]})])],"derivedFrom":makeQuery(id+"F1.opExtrude","CAP_FACE",FACE,{"disambiguationData":[OSD([subQ5,subQ7,subQ8,subQ9,subQ4,subQ3,subQ2,subQ1,subQ6,subQ0,subQ10,subQ11])],"isStart":true})});}
            var sketch = newSketch(context, id + "F16", { "sketchPlane" : qUnion([Q0])});
            skLineSegment(sketch, "E79.0", {"start": v(-70, 90) * mm, "end": v(70, 90) * mm});
            skArc(sketch, "E79.1", {"start": v(-70, 90) * mm, "mid": v(-77.07, 87.07) * mm, "end": v(-80, 80) * mm});
            skLineSegment(sketch, "E79.2", {"start": v(-80, -80) * mm, "end": v(-80, 80) * mm});
            skArc(sketch, "E79.3", {"start": v(-80, -80) * mm, "mid": v(-77.07, -87.07) * mm, "end": v(-70, -90) * mm});
            skLineSegment(sketch, "E79.4", {"start": v(-70, -90) * mm, "end": v(70, -90) * mm});
            skArc(sketch, "E79.5", {"start": v(70, -90) * mm, "mid": v(77.07, -87.07) * mm, "end": v(80, -80) * mm});
            skLineSegment(sketch, "E79.6", {"start": v(80, -80) * mm, "end": v(80, 80) * mm});
            skArc(sketch, "E79.7", {"start": v(80, 80) * mm, "mid": v(77.07, 87.07) * mm, "end": v(70, 90) * mm});
            skCircle(sketch, "E79.8", {"center": v(60, 67.5) * mm, "radius": 4 * mm});
            skCircle(sketch, "E79.9", {"center": v(-60, 67.5) * mm, "radius": 4 * mm});
            skArc(sketch, "E79.10", {"start": v(56.15, 48.18) * mm, "mid": v(0, 67.5) * mm, "end": v(-56.15, 48.18) * mm});
            skArc(sketch, "E79.11", {"start": v(-56.15, 48.18) * mm, "mid": v(-58.99, 44.68) * mm, "end": v(-60, 40.3) * mm});
            skLineSegment(sketch, "E79.12", {"start": v(-60, 40.3) * mm, "end": v(-60, -40.3) * mm});
            skArc(sketch, "E79.13", {"start": v(-56.15, -48.18) * mm, "mid": v(0, -67.5) * mm, "end": v(56.15, -48.18) * mm});
            skArc(sketch, "E79.14", {"start": v(-60, -40.3) * mm, "mid": v(-58.99, -44.68) * mm, "end": v(-56.15, -48.18) * mm});
            skCircle(sketch, "E79.15", {"center": v(-60, -67.5) * mm, "radius": 4 * mm});
            skCircle(sketch, "E79.16", {"center": v(60, -67.5) * mm, "radius": 4 * mm});
            skArc(sketch, "E79.17", {"start": v(60, 40.3) * mm, "mid": v(58.99, 44.68) * mm, "end": v(56.15, 48.18) * mm});
            skLineSegment(sketch, "E79.18", {"start": v(60, 40.3) * mm, "end": v(60, -40.3) * mm});
            skArc(sketch, "E79.19", {"start": v(56.15, -48.18) * mm, "mid": v(58.99, -44.68) * mm, "end": v(60, -40.3) * mm});
            skLineSegment(sketch, "E80", {"start": v(0, 90) * mm, "end": v(0, 120) * mm});
            skPoint(sketch, "E80.endSnap0", {"position": v(0, 90) * mm});
            skLineSegment(sketch, "E81", {"start": v(-33, 90) * mm, "end": v(-15, 108) * mm});
            skLineSegment(sketch, "E82", {"start": v(-15, 108) * mm, "end": v(-15, 120) * mm});
            skLineSegment(sketch, "E83", {"start": v(15, 108) * mm, "end": v(33, 90) * mm});
            skLineSegment(sketch, "E84", {"start": v(15, 108) * mm, "end": v(15, 120) * mm});
            skCircle(sketch, "E85", {"center": v(0, 120) * mm, "radius": 6 * mm});
            skArc(sketch, "E86", {"start": v(15, 120) * mm, "mid": v(0, 135) * mm, "end": v(-15, 120) * mm});
            skLineSegment(sketch, "E87", {"start": v(-80, 0) * mm, "end": v(80, 0) * mm, "construction": true});
            skLineSegment(sketch, "E88.MirrorCS", {"start": v(15, -108) * mm, "end": v(33, -90) * mm});
            skLineSegment(sketch, "E89.MirrorCS", {"start": v(15, -108) * mm, "end": v(15, -120) * mm});
            skArc(sketch, "E90.MirrorCS", {"start": v(15, -120) * mm, "mid": v(0, -135) * mm, "end": v(-15, -120) * mm});
            skLineSegment(sketch, "E91.MirrorCS", {"start": v(-15, -108) * mm, "end": v(-15, -120) * mm});
            skLineSegment(sketch, "E92.MirrorCS", {"start": v(-33, -90) * mm, "end": v(-15, -108) * mm});
            skLineSegment(sketch, "E93.MirrorCS", {"start": v(0, -90) * mm, "end": v(0, -120) * mm});
            skCircle(sketch, "E94.MirrorC", {"center": v(0, -120) * mm, "radius": 6 * mm});
            skSolve(sketch);
        }
        {
            var Q0;
            {var subQ11=sQuery(id+"F16.wireOp",EDGE,"E79.1");Q0=makeQuery(id+"F16.imprint","IMPRINT",FACE,{"disambiguationData":[TD([[makeQuery(id+"F16.imprint","IMPRINT",EDGE,{"derivedFrom":subQ11}),1.0]])]});}
            var Q1;
            {var subQ0=sQuery(id+"F16.wireOp",EDGE,"E81");Q1=makeQuery(id+"F16.imprint","IMPRINT",FACE,{"disambiguationData":[TD([[makeQuery(id+"F16.imprint","IMPRINT",EDGE,{"derivedFrom":subQ0}),-1.0]])]});}
            var Q2;
            {var subQ0=sQuery(id+"F16.wireOp",EDGE,"E88.MirrorCS");Q2=makeQuery(id+"F16.imprint","IMPRINT",FACE,{"disambiguationData":[TD([[makeQuery(id+"F16.imprint","IMPRINT",EDGE,{"derivedFrom":subQ0}),1.0]])]});}
            extrude(context, id + "F17", {"entities" : qUnion([Q0, Q1, Q2]), "depth" : 2.8 * mm});
        }
    });
